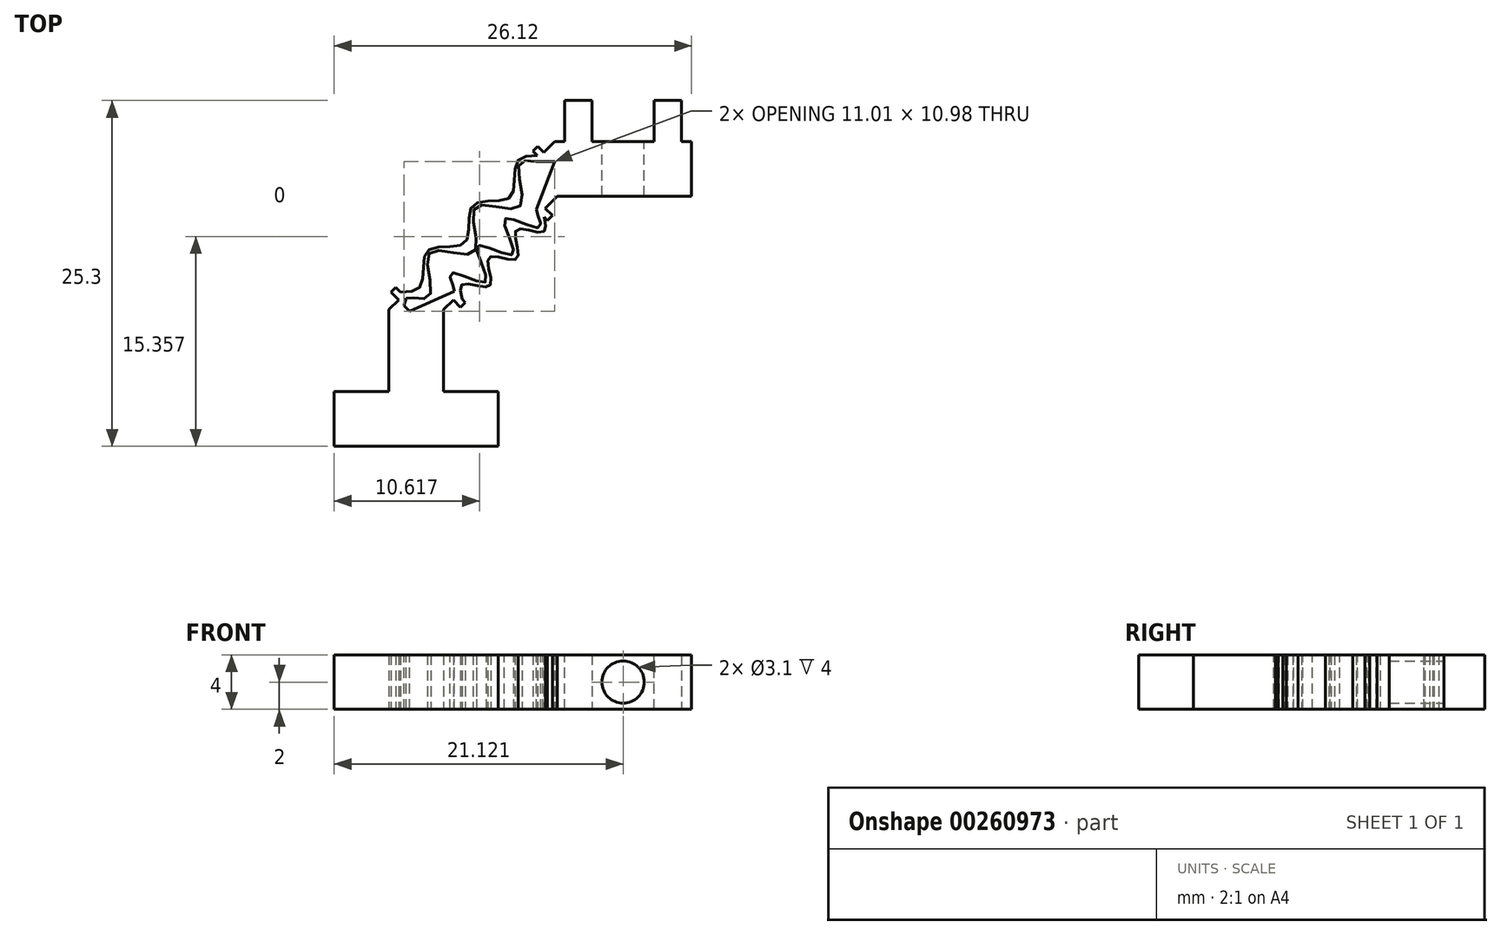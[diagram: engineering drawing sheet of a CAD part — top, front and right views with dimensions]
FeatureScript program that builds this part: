
annotation { "Feature Type Name" : "Feature", "Feature Type Description" : "" }
export const myFeature = defineFeature(function(context is Context, id is Id, definition is map)
    precondition{}
    {
        {
            var Q0;
            Q0=qCreatedBy(makeId("Top.planeOp"),FACE);
            var sketch = newSketch(context, id + "F0", { "sketchPlane" : qUnion([Q0])});
            skLineSegment(sketch, "E0", {"start": v(8, 0) * mm, "end": v(4, 0) * mm});
            skLineSegment(sketch, "E1", {"start": v(4, 4) * mm, "end": v(4, 10) * mm});
            skLineSegment(sketch, "E2", {"start": v(8, 4) * mm, "end": v(12, 4) * mm});
            skLineSegment(sketch, "E3", {"start": v(12, 4) * mm, "end": v(12, 0) * mm});
            skLineSegment(sketch, "E4", {"start": v(12, 0) * mm, "end": v(8, 0) * mm});
            skLineSegment(sketch, "E5", {"start": v(4, 0) * mm, "end": v(0, 0) * mm});
            skLineSegment(sketch, "E6", {"start": v(0, 0) * mm, "end": v(0, 4) * mm});
            skLineSegment(sketch, "E7", {"start": v(0, 4) * mm, "end": v(4, 4) * mm});
            skLineSegment(sketch, "E8", {"start": v(8, 4) * mm, "end": v(8, 10) * mm});
            skLineSegment(sketch, "E9", {"start": v(5.33, 10.8) * mm, "end": v(7, 12.46) * mm, "construction": true});
            skLineSegment(sketch, "E10", {"start": v(7, 12.46) * mm, "end": v(8.66, 14.13) * mm, "construction": true});
            skLineSegment(sketch, "E11", {"start": v(8.66, 14.13) * mm, "end": v(10.33, 15.8) * mm, "construction": true});
            skLineSegment(sketch, "E12", {"start": v(10.33, 15.8) * mm, "end": v(12, 17.46) * mm, "construction": true});
            skLineSegment(sketch, "E13", {"start": v(12, 17.46) * mm, "end": v(13.66, 19.13) * mm, "construction": true});
            skLineSegment(sketch, "E14", {"start": v(13.66, 19.13) * mm, "end": v(15.33, 20.8) * mm, "construction": true});
            skLineSegment(sketch, "E15", {"start": v(6.16, 11.63) * mm, "end": v(6.69, 11.1) * mm, "construction": true});
            skLineSegment(sketch, "E16", {"start": v(7.83, 13.3) * mm, "end": v(7.3, 13.83) * mm, "construction": true});
            skLineSegment(sketch, "E17", {"start": v(9.5, 14.96) * mm, "end": v(10.02, 14.43) * mm, "construction": true});
            skLineSegment(sketch, "E18", {"start": v(11.16, 16.63) * mm, "end": v(10.63, 17.16) * mm, "construction": true});
            skLineSegment(sketch, "E19", {"start": v(12.83, 18.3) * mm, "end": v(13.36, 17.77) * mm, "construction": true});
            skLineSegment(sketch, "E20", {"start": v(14.5, 19.96) * mm, "end": v(13.96, 20.5) * mm, "construction": true});
            skLineSegment(sketch, "E21", {"start": v(8.8, 11.33) * mm, "end": v(9.8, 12.33) * mm, "construction": true});
            skLineSegment(sketch, "E22", {"start": v(9.8, 12.33) * mm, "end": v(10.8, 13.33) * mm, "construction": true});
            skLineSegment(sketch, "E23", {"start": v(10.8, 13.33) * mm, "end": v(11.8, 14.33) * mm, "construction": true});
            skLineSegment(sketch, "E24", {"start": v(11.8, 14.33) * mm, "end": v(12.8, 15.33) * mm, "construction": true});
            skLineSegment(sketch, "E25", {"start": v(12.8, 15.33) * mm, "end": v(13.8, 16.33) * mm, "construction": true});
            skLineSegment(sketch, "E26", {"start": v(13.8, 16.33) * mm, "end": v(14.8, 17.33) * mm, "construction": true});
            skLineSegment(sketch, "E27", {"start": v(9.3, 11.83) * mm, "end": v(8.77, 12.36) * mm, "construction": true});
            skLineSegment(sketch, "E28", {"start": v(10.3, 12.83) * mm, "end": v(10.83, 12.3) * mm});
            skLineSegment(sketch, "E29", {"start": v(11.3, 13.83) * mm, "end": v(10.77, 14.36) * mm, "construction": true});
            skLineSegment(sketch, "E30", {"start": v(12.3, 14.83) * mm, "end": v(12.83, 14.3) * mm, "construction": true});
            skLineSegment(sketch, "E31", {"start": v(13.3, 15.83) * mm, "end": v(12.77, 16.36) * mm, "construction": true});
            skLineSegment(sketch, "E32", {"start": v(14.3, 16.83) * mm, "end": v(14.83, 16.3) * mm, "construction": true});
            skFitSpline(sketch, "E33", {"points": [v(5.27, 10.85) * mm, v(6.64, 11.15) * mm, v(6.94, 12.52) * mm, v(7.24, 13.88) * mm, v(8.6, 14.18) * mm, v(9.97, 14.48) * mm, v(10.27, 15.85) * mm, v(10.58, 17.21) * mm, v(11.94, 17.52) * mm, v(13.3, 17.82) * mm, v(13.6, 19.18) * mm, v(13.9, 20.55) * mm, v(15.27, 20.85) * mm], "startDerivative": vector(19.55, 0.45) * mm, "endDerivative": vector(19.55, 0.45) * mm});
            skLineSegment(sketch, "E34", {"start": v(15.33, 20.8) * mm, "end": v(14.8, 21.33) * mm});
            skFitSpline(sketch, "E35", {"points": [v(8.78, 11.34) * mm, v(8.75, 12.37) * mm, v(9.78, 12.34) * mm, v(10.8, 12.31) * mm, v(10.78, 13.34) * mm, v(10.75, 14.37) * mm, v(11.78, 14.34) * mm, v(12.8, 14.31) * mm, v(12.78, 15.34) * mm, v(12.75, 16.37) * mm, v(13.78, 16.34) * mm, v(14.8, 16.31) * mm, v(14.78, 17.34) * mm], "startDerivative": vector(-3.55, 15.55) * mm, "endDerivative": vector(-3.54, 15.55) * mm});
            skFitSpline(sketch, "E36", {"points": [v(9.34, 10.78) * mm, v(9.31, 11.8) * mm, v(10.34, 11.78) * mm, v(11.37, 11.75) * mm, v(11.34, 12.78) * mm, v(11.31, 13.8) * mm, v(12.34, 13.78) * mm, v(13.37, 13.75) * mm, v(13.34, 14.78) * mm, v(13.31, 15.8) * mm, v(14.34, 15.78) * mm, v(15.37, 15.75) * mm, v(15.34, 16.78) * mm], "startDerivative": vector(-3.55, 15.55) * mm, "endDerivative": vector(-3.54, 15.55) * mm});
            skLineSegment(sketch, "E37", {"start": v(16.3, 18.3) * mm, "end": v(26.12, 18.3) * mm});
            skLineSegment(sketch, "E38", {"start": v(26.12, 18.3) * mm, "end": v(26.12, 22.3) * mm});
            skLineSegment(sketch, "E39", {"start": v(26.12, 22.3) * mm, "end": v(16.12, 22.3) * mm});
            skLineSegment(sketch, "E40", {"start": v(8, 10) * mm, "end": v(8.88, 10.88) * mm});
            skLineSegment(sketch, "E41", {"start": v(14.53, 17.6) * mm, "end": v(14.88, 17.94) * mm});
            skLineSegment(sketch, "E42", {"start": v(15.6, 16.53) * mm, "end": v(15.94, 16.88) * mm});
            skLineSegment(sketch, "E43", {"start": v(15.94, 16.88) * mm, "end": v(14.88, 17.94) * mm});
            skLineSegment(sketch, "E44", {"start": v(15.41, 17.41) * mm, "end": v(16.3, 18.3) * mm});
            skPoint(sketch, "E45.endSnap0", {"position": v(5.46, 10.66) * mm});
            skLineSegment(sketch, "E46", {"start": v(4, 10) * mm, "end": v(4.88, 10.88) * mm});
            skLineSegment(sketch, "E47", {"start": v(15.33, 20.8) * mm, "end": v(15.41, 20.7) * mm});
            skLineSegment(sketch, "E48", {"start": v(14.8, 21.33) * mm, "end": v(14.53, 21.6) * mm});
            skLineSegment(sketch, "E49", {"start": v(14.53, 21.6) * mm, "end": v(14.88, 21.94) * mm});
            skLineSegment(sketch, "E50", {"start": v(15.41, 20.7) * mm, "end": v(15.77, 21.06) * mm});
            skLineSegment(sketch, "E51", {"start": v(14.88, 21.94) * mm, "end": v(15.77, 21.06) * mm});
            skLineSegment(sketch, "E52", {"start": v(15.33, 21.5) * mm, "end": v(16.12, 22.3) * mm});
            skLineSegment(sketch, "E53", {"start": v(14.53, 17.6) * mm, "end": v(15.6, 16.53) * mm});
            skLineSegment(sketch, "E54", {"start": v(4.5, 11.63) * mm, "end": v(5.63, 10.5) * mm});
            skLineSegment(sketch, "E55", {"start": v(4.88, 10.88) * mm, "end": v(5.06, 11.06) * mm});
            skLineSegment(sketch, "E56", {"start": v(4.8, 11.33) * mm, "end": v(5.06, 11.06) * mm});
            skLineSegment(sketch, "E57", {"start": v(5.06, 11.06) * mm, "end": v(4.85, 11.27) * mm});
            skFitSpline(sketch, "E58", {"points": [v(4.85, 11.27) * mm, v(6.21, 11.58) * mm, v(6.52, 12.94) * mm, v(6.82, 14.3) * mm, v(8.18, 14.6) * mm, v(9.55, 14.9) * mm, v(9.85, 16.27) * mm, v(10.15, 17.64) * mm, v(11.52, 17.94) * mm, v(12.88, 18.24) * mm, v(13.18, 19.6) * mm, v(13.48, 20.97) * mm, v(14.85, 21.27) * mm], "startDerivative": vector(19.55, 0.45) * mm, "endDerivative": vector(19.55, 0.45) * mm});
            skLineSegment(sketch, "E59", {"start": v(5.06, 11.06) * mm, "end": v(5.27, 10.85) * mm});
            skLineSegment(sketch, "E60", {"start": v(9.06, 11.06) * mm, "end": v(8.78, 11.34) * mm});
            skLineSegment(sketch, "E61", {"start": v(9.06, 11.06) * mm, "end": v(9.34, 10.78) * mm});
            skLineSegment(sketch, "E62", {"start": v(8.53, 11.6) * mm, "end": v(9.6, 10.53) * mm});
            skLineSegment(sketch, "E63", {"start": v(8.53, 11.6) * mm, "end": v(9.06, 11.06) * mm});
            skLineSegment(sketch, "E64", {"start": v(4.5, 11.63) * mm, "end": v(4.14, 11.27) * mm});
            skLineSegment(sketch, "E65", {"start": v(5.63, 10.5) * mm, "end": v(5.27, 10.14) * mm});
            skLineSegment(sketch, "E66", {"start": v(4.14, 11.27) * mm, "end": v(5.27, 10.14) * mm});
            skLineSegment(sketch, "E67", {"start": v(9.6, 10.53) * mm, "end": v(9.24, 10.18) * mm});
            skLineSegment(sketch, "E68", {"start": v(8.53, 11.6) * mm, "end": v(8.18, 11.24) * mm});
            skLineSegment(sketch, "E69", {"start": v(8.18, 11.24) * mm, "end": v(9.24, 10.18) * mm});
            skSolve(sketch);
        }
        {
            var Q0;
            Q0=qSketchRegion(id+"F0",true);
            extrude(context, id + "F1", {"entities" : qUnion([Q0]), "depth" : 4 * mm});
        }
        {
            var Q0;
            Q0=makeQuery(id+"F1.opExtrude","SWEPT_FACE",FACE,{"disambiguationData":[OSD([sQuery(id+"F0.wireOp",EDGE,"E39")])]});
            var sketch = newSketch(context, id + "F2", { "sketchPlane" : qUnion([Q0])});
            skLineSegment(sketch, "E70", {"start": v(-26.12, 4) * mm, "end": v(-25.4, 4) * mm});
            skLineSegment(sketch, "E71", {"start": v(-25.4, 4) * mm, "end": v(-25.4, 0) * mm});
            skLineSegment(sketch, "E72", {"start": v(-25.4, 0) * mm, "end": v(-23.4, 0) * mm});
            skLineSegment(sketch, "E73", {"start": v(-23.4, 0) * mm, "end": v(-23.4, 4) * mm});
            skLineSegment(sketch, "E74", {"start": v(-25.4, 4) * mm, "end": v(-23.4, 4) * mm});
            skLineSegment(sketch, "E75", {"start": v(-18.85, 4) * mm, "end": v(-18.85, 0) * mm});
            skLineSegment(sketch, "E76", {"start": v(-18.85, 0) * mm, "end": v(-16.85, 0) * mm});
            skLineSegment(sketch, "E77", {"start": v(-16.85, 0) * mm, "end": v(-16.85, 4) * mm});
            skLineSegment(sketch, "E78", {"start": v(-16.85, 4) * mm, "end": v(-18.85, 4) * mm});
            skSolve(sketch);
        }
        {
            var Q0;
            Q0=qSketchRegion(id+"F2",true);
            extrude(context, id + "F3", {"entities" : qUnion([Q0]), "operationType" : NewBodyOperationType.ADD, "depth" : 3 * mm});
        }
        {
            var Q0;
            {var subQ16=sQuery(id+"F0.wireOp",EDGE,"E39");Q0=makeQuery(id+"F3.boolean.opBoolean","SPLIT",FACE,{"disambiguationData":[TD([makeQuery(id+"F3.opExtrude","SWEPT_FACE",FACE,{"disambiguationData":[OSD([sQuery(id+"F2.wireOp",EDGE,"E73")])]})])],"derivedFrom":makeQuery(id+"F1.opExtrude","SWEPT_FACE",FACE,{"disambiguationData":[OSD([subQ16])]})});}
            var sketch = newSketch(context, id + "F4", { "sketchPlane" : qUnion([Q0])});
            skCircle(sketch, "E79", {"center": v(-21.12, 2) * mm, "radius": 1.55 * mm});
            skSolve(sketch);
        }
        {
            var Q0;
            Q0=qSketchRegion(id+"F4",true);
            extrude(context, id + "F5", {"entities" : qUnion([Q0]), "operationType" : NewBodyOperationType.REMOVE, "oppositeDirection" : true, "depth" : 4 * mm});
        }
        {
            var Q0;
            Q0=makeQuery(id+"F1.opExtrude","SWEPT_BODY",BODY,{"disambiguationData":[OSD([sQuery(id+"F0.wireOp",EDGE,"E0"),sQuery(id+"F0.wireOp",EDGE,"E1"),sQuery(id+"F0.wireOp",EDGE,"E2"),sQuery(id+"F0.wireOp",EDGE,"E3"),sQuery(id+"F0.wireOp",EDGE,"E4"),sQuery(id+"F0.wireOp",EDGE,"E5"),sQuery(id+"F0.wireOp",EDGE,"E6"),sQuery(id+"F0.wireOp",EDGE,"E7"),sQuery(id+"F0.wireOp",EDGE,"E8"),sQuery(id+"F0.wireOp",EDGE,"E34"),sQuery(id+"F0.wireOp",EDGE,"E36"),sQuery(id+"F0.wireOp",EDGE,"E37"),sQuery(id+"F0.wireOp",EDGE,"E38"),sQuery(id+"F0.wireOp",EDGE,"E39"),sQuery(id+"F0.wireOp",EDGE,"E40"),sQuery(id+"F0.wireOp",EDGE,"E42"),sQuery(id+"F0.wireOp",EDGE,"E43"),sQuery(id+"F0.wireOp",EDGE,"E44"),sQuery(id+"F0.wireOp",EDGE,"E46"),sQuery(id+"F0.wireOp",EDGE,"E48"),sQuery(id+"F0.wireOp",EDGE,"E49"),sQuery(id+"F0.wireOp",EDGE,"E51"),sQuery(id+"F0.wireOp",EDGE,"E52"),sQuery(id+"F0.wireOp",EDGE,"E53"),sQuery(id+"F0.wireOp",EDGE,"E54"),sQuery(id+"F0.wireOp",EDGE,"E56"),sQuery(id+"F0.wireOp",EDGE,"E58"),sQuery(id+"F0.wireOp",EDGE,"E62"),sQuery(id+"F0.wireOp",EDGE,"E64"),sQuery(id+"F0.wireOp",EDGE,"E66"),sQuery(id+"F0.wireOp",EDGE,"E67"),sQuery(id+"F0.wireOp",EDGE,"E69")])]});
            transform(context, id + "F6", {"entities" : qUnion([Q0]), "transformType" : TransformType.TRANSLATION_3D, "dx" : 0 * mm, "dy" : 0 * mm, "dz" : 0 * mm, "makeCopy" : true});
        }
        {
            var Q0;
            Q0=makeQuery(id+"F3.boolean.opBoolean","MERGE",FACE,{"derivedFrom":[makeQuery(id+"F1.opExtrude","CAP_FACE",FACE,{"disambiguationData":[OSD([sQuery(id+"F0.wireOp",EDGE,"E0"),sQuery(id+"F0.wireOp",EDGE,"E1"),sQuery(id+"F0.wireOp",EDGE,"E2"),sQuery(id+"F0.wireOp",EDGE,"E3"),sQuery(id+"F0.wireOp",EDGE,"E4"),sQuery(id+"F0.wireOp",EDGE,"E5"),sQuery(id+"F0.wireOp",EDGE,"E6"),sQuery(id+"F0.wireOp",EDGE,"E7"),sQuery(id+"F0.wireOp",EDGE,"E8"),sQuery(id+"F0.wireOp",EDGE,"E34"),sQuery(id+"F0.wireOp",EDGE,"E36"),sQuery(id+"F0.wireOp",EDGE,"E37"),sQuery(id+"F0.wireOp",EDGE,"E38"),sQuery(id+"F0.wireOp",EDGE,"E39"),sQuery(id+"F0.wireOp",EDGE,"E40"),sQuery(id+"F0.wireOp",EDGE,"E42"),sQuery(id+"F0.wireOp",EDGE,"E43"),sQuery(id+"F0.wireOp",EDGE,"E44"),sQuery(id+"F0.wireOp",EDGE,"E46"),sQuery(id+"F0.wireOp",EDGE,"E48"),sQuery(id+"F0.wireOp",EDGE,"E49"),sQuery(id+"F0.wireOp",EDGE,"E51"),sQuery(id+"F0.wireOp",EDGE,"E52"),sQuery(id+"F0.wireOp",EDGE,"E53"),sQuery(id+"F0.wireOp",EDGE,"E54"),sQuery(id+"F0.wireOp",EDGE,"E56"),sQuery(id+"F0.wireOp",EDGE,"E58"),sQuery(id+"F0.wireOp",EDGE,"E62"),sQuery(id+"F0.wireOp",EDGE,"E64"),sQuery(id+"F0.wireOp",EDGE,"E66"),sQuery(id+"F0.wireOp",EDGE,"E67"),sQuery(id+"F0.wireOp",EDGE,"E69")])],"isStart":false}),makeQuery(id+"F3.opExtrude","SWEPT_FACE",FACE,{"disambiguationData":[OSD([sQuery(id+"F2.wireOp",EDGE,"E74")])]}),makeQuery(id+"F3.opExtrude","SWEPT_FACE",FACE,{"disambiguationData":[OSD([sQuery(id+"F2.wireOp",EDGE,"E78")])]})]});
            var sketch = newSketch(context, id + "F7", { "sketchPlane" : qUnion([Q0])});
            skFitSpline(sketch, "E80.0", {"points": [v(5.27, 10.85) * mm, v(5.82, 10.86) * mm, v(6.9, 10.89) * mm, v(6.94, 12.52) * mm, v(6.98, 14.14) * mm, v(8.6, 14.18) * mm, v(10.23, 14.22) * mm, v(10.27, 15.85) * mm, v(10.31, 17.48) * mm, v(11.94, 17.52) * mm, v(13.57, 17.55) * mm, v(13.6, 19.18) * mm, v(13.64, 20.81) * mm, v(14.73, 20.84) * mm, v(15.27, 20.85) * mm]});
            skFitSpline(sketch, "E80.1", {"points": [v(8.78, 11.34) * mm, v(8.68, 11.78) * mm, v(8.48, 12.64) * mm, v(9.78, 12.34) * mm, v(11.07, 12.05) * mm, v(10.78, 13.34) * mm, v(10.48, 14.64) * mm, v(11.78, 14.34) * mm, v(13.07, 14.05) * mm, v(12.78, 15.34) * mm, v(12.48, 16.64) * mm, v(13.78, 16.34) * mm, v(15.07, 16.05) * mm, v(14.88, 16.91) * mm, v(14.78, 17.34) * mm]});
            skLineSegment(sketch, "E81", {"start": v(15.27, 20.85) * mm, "end": v(16.12, 20.85) * mm});
            skLineSegment(sketch, "E82", {"start": v(14.78, 17.34) * mm, "end": v(16.12, 20.85) * mm});
            skLineSegment(sketch, "E83", {"start": v(5.52, 9.87) * mm, "end": v(8.78, 11.34) * mm});
            skLineSegment(sketch, "E84", {"start": v(5.52, 9.87) * mm, "end": v(5.11, 10.28) * mm});
            skLineSegment(sketch, "E85", {"start": v(5.11, 10.28) * mm, "end": v(5.27, 10.85) * mm});
            skSolve(sketch);
        }
        {
            var Q0;
            Q0 = qSketchRegion(id + "F7", true);
            extrude(context, id + "F8", {"entities" : qUnion([Q0]), "operationType" : NewBodyOperationType.REMOVE, "oppositeDirection" : true, "depth" : 4 * mm});
        }
    });
